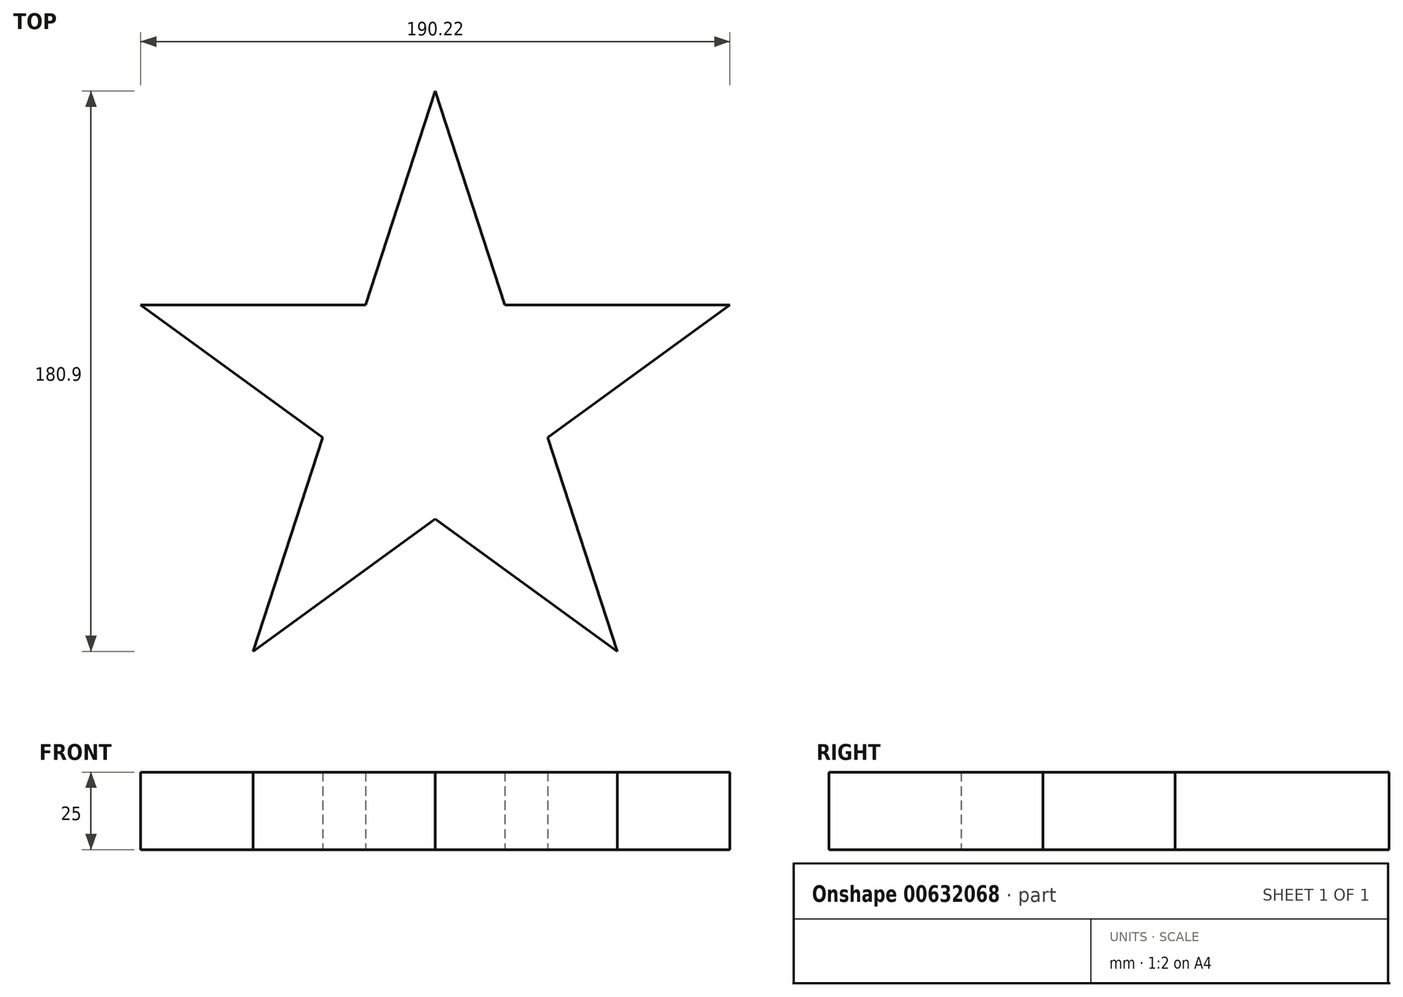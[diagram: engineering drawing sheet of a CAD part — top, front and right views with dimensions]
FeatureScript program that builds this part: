
annotation { "Feature Type Name" : "Feature", "Feature Type Description" : "" }
export const myFeature = defineFeature(function(context is Context, id is Id, definition is map)
    precondition{}
    {
        {
            var Q0;
            Q0=qCreatedBy(makeId("Top.planeOp"),FACE);
            var sketch = newSketch(context, id + "F0", { "sketchPlane" : qUnion([Q0])});
            skLineSegment(sketch, "E0", {"start": v(0, 0) * mm, "end": v(0, 144.27) * mm, "construction": true});
            skLineSegment(sketch, "E1", {"start": v(0, 0) * mm, "end": v(153.16, 49.76) * mm, "construction": true});
            skLineSegment(sketch, "E2", {"start": v(0, 0) * mm, "end": v(87.85, -120.92) * mm, "construction": true});
            skLineSegment(sketch, "E3", {"start": v(0, 0) * mm, "end": v(-98.53, -135.61) * mm, "construction": true});
            skLineSegment(sketch, "E4", {"start": v(0, 0) * mm, "end": v(-160.96, 52.3) * mm, "construction": true});
            skPoint(sketch, "E5", {"position": v(0, 100) * mm});
            skPoint(sketch, "E6", {"position": v(95.1, 30.9) * mm});
            skPoint(sketch, "E7", {"position": v(58.78, -80.9) * mm});
            skPoint(sketch, "E8", {"position": v(-58.78, -80.9) * mm});
            skPoint(sketch, "E9", {"position": v(-95.1, 30.9) * mm});
            skLineSegment(sketch, "E10", {"start": v(-58.78, -80.9) * mm, "end": v(0, -38.2) * mm});
            skLineSegment(sketch, "E11", {"start": v(-58.78, -80.9) * mm, "end": v(-36.33, -11.8) * mm});
            skLineSegment(sketch, "E12", {"start": v(-95.1, 30.9) * mm, "end": v(-22.45, 30.9) * mm});
            skLineSegment(sketch, "E13", {"start": v(0, 100) * mm, "end": v(22.45, 30.9) * mm});
            skLineSegment(sketch, "E14", {"start": v(58.78, -80.9) * mm, "end": v(0, -38.2) * mm});
            skLineSegment(sketch, "E15.trimOffspring", {"start": v(-22.45, 30.9) * mm, "end": v(0, 100) * mm});
            skLineSegment(sketch, "E16.trimOffspring", {"start": v(-36.33, -11.8) * mm, "end": v(-95.1, 30.9) * mm});
            skLineSegment(sketch, "E17.trimOffspring", {"start": v(36.33, -11.8) * mm, "end": v(95.1, 30.9) * mm});
            skLineSegment(sketch, "E18.trimOffspring", {"start": v(36.33, -11.8) * mm, "end": v(58.78, -80.9) * mm});
            skLineSegment(sketch, "E19.trimOffspring", {"start": v(22.45, 30.9) * mm, "end": v(95.1, 30.9) * mm});
            skSolve(sketch);
        }
        {
            var Q0;
            Q0 = qSketchRegion(id + "F0", true);
            extrude(context, id + "F1", {"entities" : qUnion([Q0]), "depth" : 25 * mm, "offsetDistance" : 25 * mm});
        }
    });
